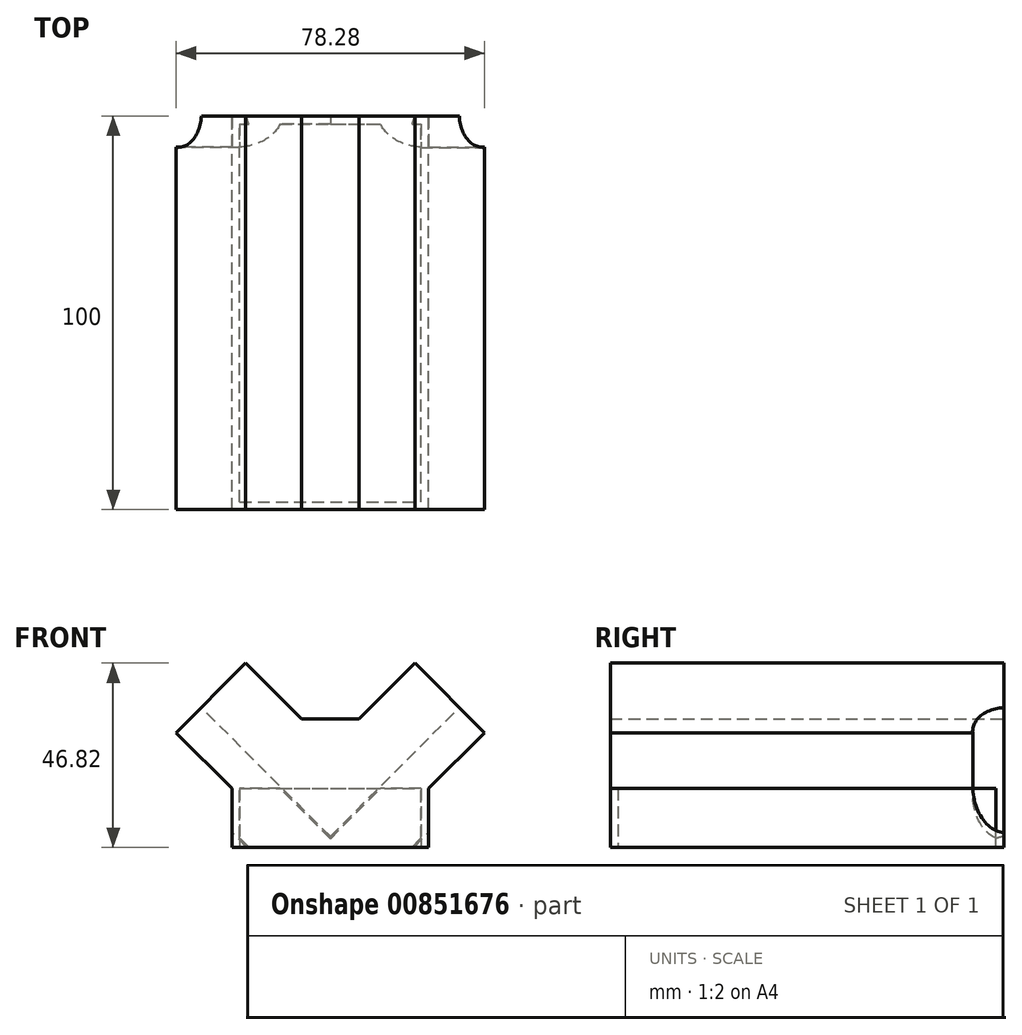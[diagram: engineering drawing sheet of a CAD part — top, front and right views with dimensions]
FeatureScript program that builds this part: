
annotation { "Feature Type Name" : "Feature", "Feature Type Description" : "" }
export const myFeature = defineFeature(function(context is Context, id is Id, definition is map)
    precondition{}
    {
        {
            var Q0;
            Q0=qCreatedBy(makeId("Front.planeOp"),FACE);
            var sketch = newSketch(context, id + "F0", { "sketchPlane" : qUnion([Q0])});
            skLineSegment(sketch, "E0", {"start": v(0, -8.44) * mm, "end": v(25, -8.44) * mm});
            skLineSegment(sketch, "E1", {"start": v(25, -8.44) * mm, "end": v(25, 6.56) * mm});
            skLineSegment(sketch, "E2", {"start": v(25, 6.56) * mm, "end": v(39.14, 20.7) * mm});
            skLineSegment(sketch, "E3", {"start": v(39.14, 20.7) * mm, "end": v(21.46, 38.38) * mm});
            skLineSegment(sketch, "E4", {"start": v(21.46, 38.38) * mm, "end": v(7.32, 24.24) * mm});
            skLineSegment(sketch, "E5", {"start": v(7.32, 24.24) * mm, "end": v(0, 24.24) * mm});
            skLineSegment(sketch, "E6", {"start": v(0, 60.02) * mm, "end": v(0, -64.68) * mm, "construction": true});
            skLineSegment(sketch, "E7.MirrorCS", {"start": v(-7.32, 24.24) * mm, "end": v(0, 24.24) * mm});
            skLineSegment(sketch, "E8.MirrorCS", {"start": v(-21.46, 38.38) * mm, "end": v(-7.32, 24.24) * mm});
            skLineSegment(sketch, "E9.MirrorCS", {"start": v(-39.14, 20.7) * mm, "end": v(-21.46, 38.38) * mm});
            skLineSegment(sketch, "E10.MirrorCS", {"start": v(-25, 6.56) * mm, "end": v(-39.14, 20.7) * mm});
            skLineSegment(sketch, "E11.MirrorCS", {"start": v(-25, -8.44) * mm, "end": v(-25, 6.56) * mm});
            skLineSegment(sketch, "E12.MirrorCS", {"start": v(0, -8.44) * mm, "end": v(-25, -8.44) * mm});
            skSolve(sketch);
        }
        {
            var Q0;
            Q0=makeQuery(id+"F0.imprint","IMPRINT",FACE,{"disambiguationData":[TD([[makeQuery(id+"F0.imprint","IMPRINT",EDGE,{"derivedFrom":sQuery(id+"F0.wireOp",EDGE,"E0")}),1.0]])]});
            extrude(context, id + "F1", {"entities" : qUnion([Q0]), "depth" : 100 * mm, "offsetDistance" : 25 * mm});
        }
        {
            var Q0;
            Q0=makeQuery(id+"F1.opExtrude","SWEPT_FACE",FACE,{"disambiguationData":[OSD([sQuery(id+"F0.wireOp",EDGE,"E0"),sQuery(id+"F0.wireOp",EDGE,"E12.MirrorCS")])]});
            var sketch = newSketch(context, id + "F2", { "sketchPlane" : qUnion([Q0])});
            skLineSegment(sketch, "E13.bottom", {"start": v(-23, 98) * mm, "end": v(23, 98) * mm});
            skLineSegment(sketch, "E13.top", {"start": v(-23, 2) * mm, "end": v(23, 2) * mm});
            skLineSegment(sketch, "E13.left", {"start": v(-23, 98) * mm, "end": v(-23, 2) * mm});
            skLineSegment(sketch, "E13.right", {"start": v(23, 98) * mm, "end": v(23, 2) * mm});
            skSolve(sketch);
        }
        {
            var Q0;
            Q0=makeQuery(id+"F2.imprint","IMPRINT",FACE,{"disambiguationData":[TD([[makeQuery(id+"F2.imprint","IMPRINT",EDGE,{"derivedFrom":sQuery(id+"F2.wireOp",EDGE,"E13.bottom")}),-1.0]])]});
            extrude(context, id + "F3", {"entities" : qUnion([Q0]), "operationType" : NewBodyOperationType.REMOVE, "oppositeDirection" : true, "depth" : 15 * mm, "offsetDistance" : 25 * mm});
        }
        {
            var Q0;
            Q0=makeQuery(id+"F1.opExtrude","SWEPT_FACE",FACE,{"disambiguationData":[OSD([sQuery(id+"F0.wireOp",EDGE,"E3")])]});
            var sketch = newSketch(context, id + "F4", { "sketchPlane" : qUnion([Q0])});
            skLineSegment(sketch, "E14", {"start": v(0.54, -100) * mm, "end": v(0.54, 0) * mm, "construction": true});
            skLineSegment(sketch, "E15", {"start": v(-1.07, -12.5) * mm, "end": v(3.59, -12.5) * mm, "construction": true});
            skLineSegment(sketch, "E16", {"start": v(-0.05, -87.5) * mm, "end": v(4.61, -87.5) * mm, "construction": true});
            skLineSegment(sketch, "E17", {"start": v(-2.28, -62.5) * mm, "end": v(6.94, -62.5) * mm, "construction": true});
            skLineSegment(sketch, "E18", {"start": v(-1.82, -37.5) * mm, "end": v(2.84, -37.5) * mm, "construction": true});
            skCircle(sketch, "E19", {"center": v(-0.05, -87.5) * mm, "radius": 8.5 * mm});
            skCircle(sketch, "E20", {"center": v(0.54, -62.5) * mm, "radius": 8.5 * mm});
            skCircle(sketch, "E21", {"center": v(0.54, -37.5) * mm, "radius": 8.5 * mm});
            skCircle(sketch, "E22", {"center": v(0.54, -12.5) * mm, "radius": 8.5 * mm});
            skLineSegment(sketch, "E23", {"start": v(-42.23, -120.08) * mm, "end": v(-42.23, 17.85) * mm, "construction": true});
            skSolve(sketch);
        }
        {
            var Q0;
            Q0=makeQuery(id+"F4.imprint","IMPRINT",FACE,{"disambiguationData":[TD([[makeQuery(id+"F4.imprint","IMPRINT",EDGE,{"derivedFrom":sQuery(id+"F4.wireOp",EDGE,"E19")}),1.0]])]});
            var Q1;
            Q1=makeQuery(id+"F4.imprint","IMPRINT",FACE,{"disambiguationData":[TD([[makeQuery(id+"F4.imprint","IMPRINT",EDGE,{"derivedFrom":sQuery(id+"F4.wireOp",EDGE,"E20")}),1.0]])]});
            var Q2;
            Q2=makeQuery(id+"F4.imprint","IMPRINT",FACE,{"disambiguationData":[TD([[makeQuery(id+"F4.imprint","IMPRINT",EDGE,{"derivedFrom":sQuery(id+"F4.wireOp",EDGE,"E21")}),1.0]])]});
            var Q3;
            Q3=makeQuery(id+"F4.imprint","IMPRINT",FACE,{"disambiguationData":[TD([[makeQuery(id+"F4.imprint","IMPRINT",EDGE,{"derivedFrom":sQuery(id+"F4.wireOp",EDGE,"E22")}),1.0]])]});
            extrude(context, id + "F5", {"entities" : qUnion([Q0, Q1, Q2, Q3]), "operationType" : NewBodyOperationType.REMOVE, "oppositeDirection" : true, "depth" : 50.2 * mm, "offsetDistance" : 25 * mm});
        }
        {
            var Q0;
            Q0=makeQuery(id+"F1.opExtrude","SWEPT_FACE",FACE,{"disambiguationData":[OSD([sQuery(id+"F0.wireOp",EDGE,"E9.MirrorCS")])]});
            var sketch = newSketch(context, id + "F6", { "sketchPlane" : qUnion([Q0])});
            skLineSegment(sketch, "E24", {"start": v(57.96, -496.52) * mm, "end": v(49.87, -498.32) * mm, "construction": true});
            skLineSegment(sketch, "E25", {"start": v(-0.54, -100) * mm, "end": v(-0.54, 5.87) * mm, "construction": true});
            skLineSegment(sketch, "E26", {"start": v(1.7, -12.5) * mm, "end": v(-3.06, -12.5) * mm, "construction": true});
            skLineSegment(sketch, "E27", {"start": v(1.98, -37.5) * mm, "end": v(-2.4, -37.5) * mm, "construction": true});
            skLineSegment(sketch, "E28", {"start": v(2.35, -62.5) * mm, "end": v(-3.7, -62.5) * mm, "construction": true});
            skLineSegment(sketch, "E29", {"start": v(1.7, -87.5) * mm, "end": v(-3.15, -87.5) * mm});
            skCircle(sketch, "E30", {"center": v(-0.54, -12.5) * mm, "radius": 8.5 * mm});
            skCircle(sketch, "E31", {"center": v(-0.54, -37.5) * mm, "radius": 8.5 * mm});
            skCircle(sketch, "E32", {"center": v(-0.54, -62.5) * mm, "radius": 8.5 * mm});
            skCircle(sketch, "E33", {"center": v(-0.54, -87.5) * mm, "radius": 8.5 * mm});
            skSolve(sketch);
        }
        {
            var Q0;
            Q0=makeQuery(id+"F6.imprint","IMPRINT",FACE,{"disambiguationData":[TD([[makeQuery(id+"F6.imprint","IMPRINT",EDGE,{"derivedFrom":sQuery(id+"F6.wireOp",EDGE,"E30")}),1.0]])]});
            var Q1;
            Q1=makeQuery(id+"F6.imprint","IMPRINT",FACE,{"disambiguationData":[TD([[makeQuery(id+"F6.imprint","IMPRINT",EDGE,{"derivedFrom":sQuery(id+"F6.wireOp",EDGE,"E31")}),1.0]])]});
            var Q2;
            Q2=makeQuery(id+"F6.imprint","IMPRINT",FACE,{"disambiguationData":[TD([[makeQuery(id+"F6.imprint","IMPRINT",EDGE,{"derivedFrom":sQuery(id+"F6.wireOp",EDGE,"E32")}),1.0]])]});
            var Q3;
            Q3=makeQuery(id+"F6.imprint","IMPRINT",FACE,{"disambiguationData":[TD([[makeQuery(id+"F6.imprint","IMPRINT",EDGE,{"derivedFrom":sQuery(id+"F6.wireOp",EDGE,"E33")}),1.0]])]});
            extrude(context, id + "F7", {"entities" : qUnion([Q0, Q1, Q2, Q3]), "operationType" : NewBodyOperationType.REMOVE, "oppositeDirection" : true, "depth" : 63.4 * mm, "offsetDistance" : 25 * mm});
        }
    });
